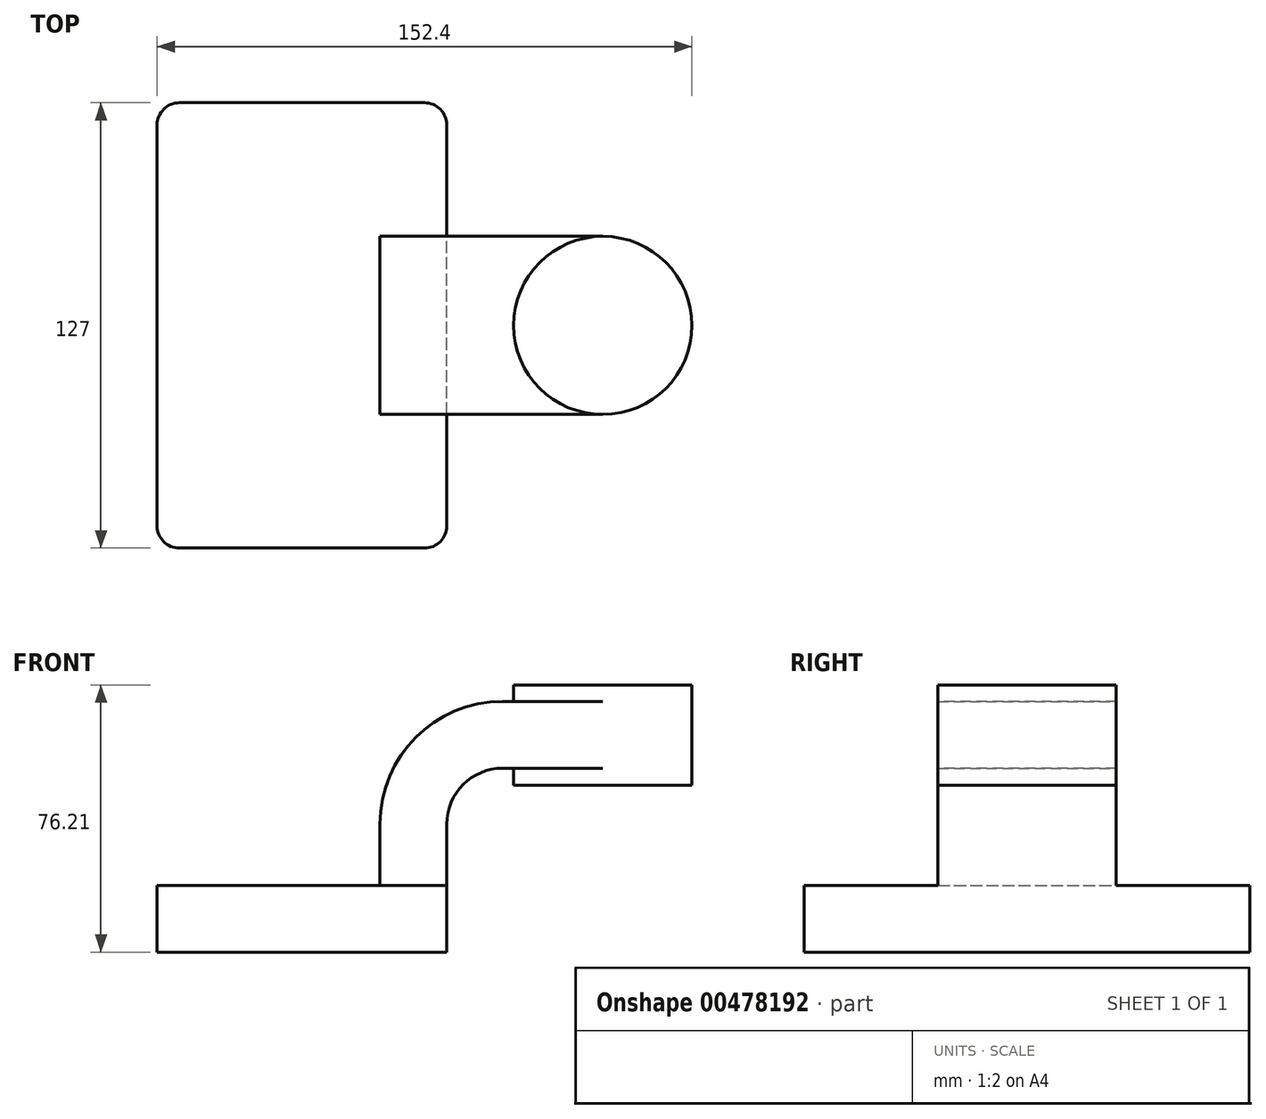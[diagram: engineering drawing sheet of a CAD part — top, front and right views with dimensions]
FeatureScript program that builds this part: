
annotation { "Feature Type Name" : "Feature", "Feature Type Description" : "" }
export const myFeature = defineFeature(function(context is Context, id is Id, definition is map)
    precondition{}
    {
        {
            var Q0;
            Q0=qCreatedBy(makeId("Front.planeOp"),FACE);
            var sketch = newSketch(context, id + "F0", { "sketchPlane" : qUnion([Q0])});
            skLineSegment(sketch, "E0.bottom", {"start": v(41.28, -9.52) * mm, "end": v(-41.27, -9.53) * mm});
            skLineSegment(sketch, "E0.top", {"start": v(41.27, 9.53) * mm, "end": v(-41.28, 9.53) * mm});
            skLineSegment(sketch, "E0.left", {"start": v(41.28, -9.52) * mm, "end": v(41.28, 9.53) * mm});
            skLineSegment(sketch, "E0.right", {"start": v(-41.27, -9.53) * mm, "end": v(-41.28, 9.53) * mm});
            skPoint(sketch, "E0.middle", {"position": v(0, 0) * mm});
            skLineSegment(sketch, "E1.bottom", {"start": v(60.32, 38.1) * mm, "end": v(111.12, 38.1) * mm});
            skLineSegment(sketch, "E1.top", {"start": v(60.32, 66.68) * mm, "end": v(111.12, 66.68) * mm});
            skLineSegment(sketch, "E1.left", {"start": v(60.32, 38.1) * mm, "end": v(60.32, 66.68) * mm});
            skLineSegment(sketch, "E1.right", {"start": v(111.12, 38.1) * mm, "end": v(111.12, 66.68) * mm});
            skPoint(sketch, "E1.middle", {"position": v(85.72, 52.39) * mm});
            skLineSegment(sketch, "E2", {"start": v(41.27, 9.53) * mm, "end": v(41.27, 27.01) * mm});
            skArc(sketch, "E3", {"start": v(41.27, 27.01) * mm, "mid": v(45.92, 38.24) * mm, "end": v(57.15, 42.89) * mm});
            skLineSegment(sketch, "E4.0", {"start": v(57.15, 61.94) * mm, "end": v(85.72, 61.94) * mm});
            skArc(sketch, "E4.1", {"start": v(22.23, 27.01) * mm, "mid": v(32.45, 51.7) * mm, "end": v(57.15, 61.94) * mm});
            skLineSegment(sketch, "E4.2", {"start": v(22.23, 9.53) * mm, "end": v(22.23, 27.01) * mm});
            skPoint(sketch, "E5.endSnap0", {"position": v(85.72, 38.1) * mm});
            skPoint(sketch, "E5.endSnap1", {"position": v(45.92, 38.24) * mm});
            skFitSpline(sketch, "E6", {"points": [v(57.15, 61.94) * mm, v(-41.28, 9.53) * mm], "startDerivative": vector(-122.7, 4.11) * mm, "endDerivative": vector(-47.4, -146.76) * mm});
            skLineSegment(sketch, "E7", {"start": v(57.15, 42.89) * mm, "end": v(85.72, 42.89) * mm});
            skLineSegment(sketch, "E8", {"start": v(85.72, 66.68) * mm, "end": v(85.72, 38.1) * mm});
            skSolve(sketch);
        }
        {
            var Q0;
            Q0=makeQuery(id+"F0.imprint","IMPRINT",FACE,{"disambiguationData":[TD([[makeQuery(id+"F0.imprint","IMPRINT",EDGE,{"derivedFrom":sQuery(id+"F0.wireOp",EDGE,"E0.bottom")}),-1.0]])]});
            extrude(context, id + "F1", {"entities" : qUnion([Q0]), "endBound" : BoundingType.SYMMETRIC, "depth" : 127 * mm});
        }
        {
            var Q0;
            {var subQ0=sQuery(id+"F0.wireOp",EDGE,"E7");var subQ1=sQuery(id+"F0.wireOp",EDGE,"E1.left");var subQ2=makeQuery(id+"F0.imprint","INTERSECT",VERTEX,{"derivedFrom":[subQ1,subQ0]});Q0=makeQuery(id+"F0.imprint","IMPRINT",FACE,{"disambiguationData":[TD([[makeQuery(id+"F0.imprint","IMPRINT",EDGE,{"disambiguationData":[TD([[subQ2,-1.0]])],"derivedFrom":subQ1}),-1.0]])]});}
            var Q1;
            {var subQ1=sQuery(id+"F0.wireOp",EDGE,"E2");Q1=makeQuery(id+"F0.imprint","IMPRINT",FACE,{"disambiguationData":[TD([[makeQuery(id+"F0.imprint","IMPRINT",EDGE,{"derivedFrom":subQ1}),1.0]])]});}
            extrude(context, id + "F2", {"entities" : qUnion([Q0, Q1]), "operationType" : NewBodyOperationType.ADD, "endBound" : BoundingType.SYMMETRIC, "depth" : 50.8 * mm});
        }
        {
            var Q0;
            Q0=makeQuery(id+"F0.imprint","IMPRINT",FACE,{"disambiguationData":[TD([[makeQuery(id+"F0.imprint","IMPRINT",EDGE,{"derivedFrom":sQuery(id+"F0.wireOp",EDGE,"E4.1")}),1.0]])]});
            extrude(context, id + "F3", {"entities" : qUnion([Q0]), "operationType" : NewBodyOperationType.ADD, "endBound" : BoundingType.SYMMETRIC, "depth" : 12.7 * mm});
        }
        {
            var Q0;
            {var subQ4=sQuery(id+"F0.wireOp",EDGE,"E1.right");Q0=makeQuery(id+"F0.imprint","IMPRINT",FACE,{"disambiguationData":[TD([[makeQuery(id+"F0.imprint","IMPRINT",EDGE,{"derivedFrom":subQ4}),1.0]])]});}
            var Q1;
            Q1=sQuery(id+"F0.wireOp",EDGE,"E8");
            revolve(context, id + "F4", {"operationType" : NewBodyOperationType.ADD, "entities" : qUnion([Q0]), "axis" : qUnion([Q1]), "revolveType" : RevolveType.FULL});
        }
        {
            var Q0;
            Q0=makeQuery(id+"F1.opExtrude","CAP_EDGE",EDGE,{"disambiguationData":[OSD([sQuery(id+"F0.wireOp",EDGE,"E0.left")])],"isStart":false});
            var Q1;
            Q1=makeQuery(id+"F1.opExtrude","CAP_EDGE",EDGE,{"disambiguationData":[OSD([sQuery(id+"F0.wireOp",EDGE,"E0.right")])],"isStart":false});
            var Q2;
            Q2=makeQuery(id+"F1.opExtrude","CAP_EDGE",EDGE,{"disambiguationData":[OSD([sQuery(id+"F0.wireOp",EDGE,"E0.right")])],"isStart":true});
            var Q3;
            Q3=makeQuery(id+"F1.opExtrude","CAP_EDGE",EDGE,{"disambiguationData":[OSD([sQuery(id+"F0.wireOp",EDGE,"E0.left")])],"isStart":true});
            fillet(context, id + "F5", {"entities" : qUnion([Q0, Q1, Q2, Q3]), "radius" : 6.35 * mm, "tangentPropagation" : true, "allowEdgeOverflow" : false});
        }
    });
